# Revit family: 63_UN_LEDPanel_RTP-XM 595x595 2-Lamps_Norton
name_source: partatom
category: Lighting Fixtures
units: mm (PartAtom-declared; Revit-internal decimal feet)

## family parameters
Always vertical = Yes
Cut with Voids When Loaded = No
Light Source = Yes
OmniClass Number = 23.80.70.11.14.11
OmniClass Title = Downlights
Part Type = Normal
Room Calculation Point = Yes
Round Connector Dimension = Use Diameter
Shared = No
Work Plane-Based = No

## types (2) — shared parameters
Assembly Code = 63.0
Calc_L1_Symbol = 6 mm  [stored 0.019685 ft]
Calc_L2_Symbol = 6 mm  [stored 0.019685 ft]
Color Filter = 16777215
Dimming Lamp Color Temperature Shift = <None>
ETIM Code = -
Emit Shape Visible in Rendering = No
Emit from Rectangle Length = 574 mm  [stored 1.8832 ft]
Emit from Rectangle Width = 574 mm  [stored 1.8832 ft]
GTIN Code = -
H1 = 48 mm  [stored 0.15748 ft]
Housing_Material = Laminate, White
IK Value = IK07
IP Value = IP20
ISBN Code = -
IfcExportAs = IfcLightFixtureType
IfcExportType = USERDEFINED
L1 = 596 mm
L2 = 596 mm
L3 = 11 mm
Lamp = LED
Manufacturer = Norton
Model = RTP XM
Tilt Angle = 90.00°
Type Comments = 60x60
URL = https://www.ivlibrary.com
Voltage = 230 V

## per-type parameters (varying)
| type | Apparent Load | Luminous Flux (lm) | Photometric Web File | Wattage Comments |
| RTP-XM LED 83 2 3800LM GST 60x60 | 38 VA | 3800 lm | RTPXMLED832LM380060x60_LDT.ies | 38W |
| RTP-XM LED 84 2 4000LM GST 60x60 | 36 VA | 4000 lm | RTPXMLED842LM400060x60_LDT.ies | 36W |

note: [stored X ft] marks values corroborated as IEEE doubles in the binary element streams (Revit-internal decimal feet)

## geometry (parser evidence)
native form markers: Sweep x3
no freeform markers — native parametric forms only
